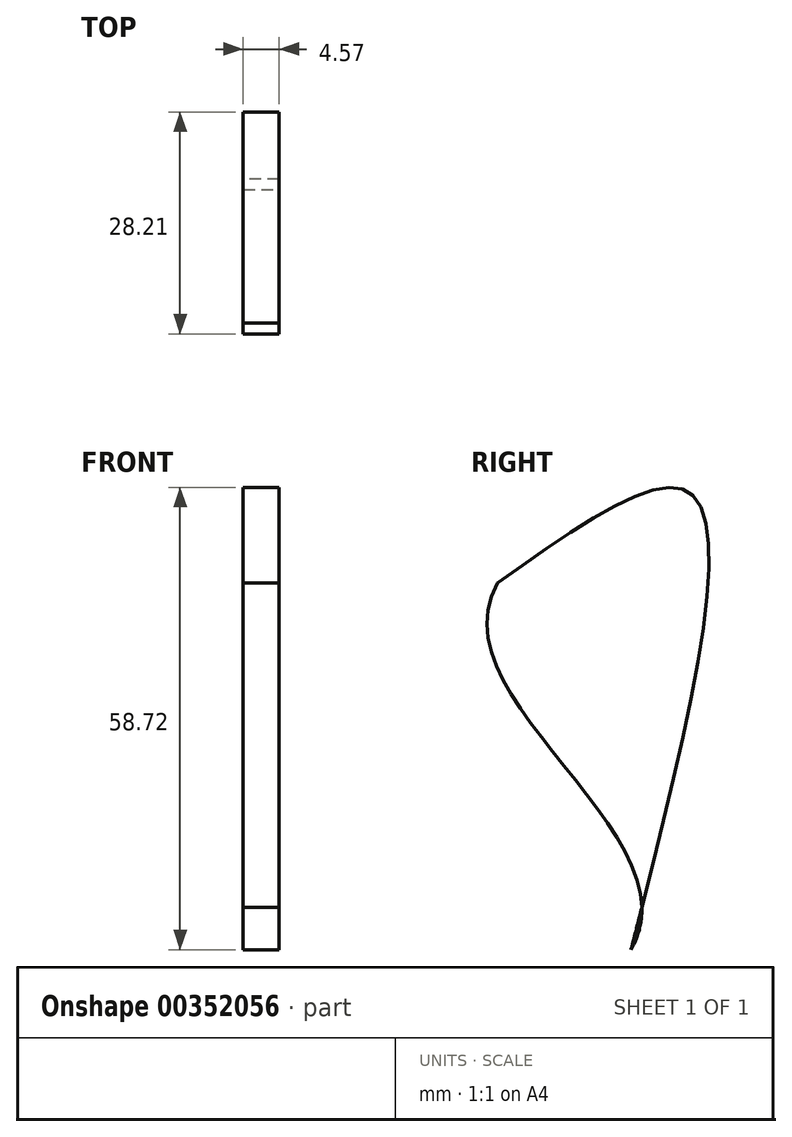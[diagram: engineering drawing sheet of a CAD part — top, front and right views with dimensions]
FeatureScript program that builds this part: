
annotation { "Feature Type Name" : "Feature", "Feature Type Description" : "" }
export const myFeature = defineFeature(function(context is Context, id is Id, definition is map)
    precondition{}
    {
        {
            var Q0;
            Q0=qCreatedBy(makeId("Right.planeOp"),FACE);
            var sketch = newSketch(context, id + "F0", { "sketchPlane" : qUnion([Q0])});
            skFitSpline(sketch, "E0", {"points": [v(0, 0) * mm, v(-16.95, 46.6) * mm], "startDerivative": vector(25.33, 44.72) * mm, "endDerivative": vector(25.33, 44.72) * mm});
            skFitSpline(sketch, "E1", {"points": [v(-16.95, 46.6) * mm, v(7.51, 58) * mm, v(0, 0) * mm], "startDerivative": vector(75.24, 53.57) * mm, "endDerivative": vector(-34.37, -134.78) * mm});
            skSolve(sketch);
        }
        {
            var Q0;
            Q0 = qSketchRegion(id + "F0", true);
            extrude(context, id + "F1", {"entities" : qUnion([Q0]), "depth" : 4.57 * mm});
        }
    });
